# Revit family: Bath-Alcove-KOHLER-Expanse-K-1100
name_source: partatom
category: Plumbing Fixtures
units: mm (PartAtom-declared; Revit-internal decimal feet)

## family parameters
Cut with Voids When Loaded = No
Host = Face
OmniClass Number = 23.31.15.00
OmniClass Title = Bathtubs
Part Type = Normal
Room Calculation Point = No
Round Connector Dimension = Use Diameter
Shared = No

## types (4) — shared parameters
ADA Compliant = No
Assembly Code = D2010500
CW Connection = No
Cold Water Inlet = Cold Water Inlet
Date Modified = 08/16/2022
Default Elevation = 0"
Drain Included = No
HW Connection = No
Height = 18 1/4"
Hot Water Inlet = Hot Water Inlet
Length = 60"
Manufacturer = Kohler Co.
Master Format 2014 = 22 41 19
Master Format 2014 Name = Residential Bathtubs
Material = Acrylic
Product Documentation Link = https://www.us.kohler.com
Product Name = Expanse
Product Page URL = https://www.us.kohler.com
URL = https://www.us.kohler.com
Vent Connection = No
Waste Connection = Yes
Waste Water Outlet = Waste Water Outlet
WaterSense Certified = No
Width = 38 1/16"

## per-type parameters (varying)
| type | Connector Distance | Description | Finish | Left Hand Drain | Model | Right Hand Drain | Type |
| Left Drain, 0-White | 40 1/2" | 60 Inch x 32 Inch curved alcove bath with integral flange and left-hand drain | KOHLER-Acrylic-0-White | Yes | K-1100-LA-0 | No | 1 |
| Left Drain, 96-Biscuit | 40 1/2" | 60 Inch x 32 Inch curved alcove bath with integral flange and left-hand drain | KOHLER-Acrylic-96-Biscuit | Yes | K-1100-LA-96 | No | 2 |
| Right Drain, 0-White | 0" | 60 Inch x 32 Inch alcove bath with curved integral apron and right-hand drain | KOHLER-Acrylic-0-White | No | K-1100-RA-0 | Yes | 3 |
| Right Drain, 96-Biscuit | 0" | 60 Inch x 32 Inch alcove bath with curved integral apron and right-hand drain | KOHLER-Acrylic-96-Biscuit | No | K-1100-RA-96 | Yes | 4 |

## geometry (parser evidence)
native form markers: Sweep x6
no freeform markers — native parametric forms only
